# Revit family: CHECK ANTIRETORNO
name_source: partatom
category: Pipe Accessories
units: mm (PartAtom-declared; Revit-internal decimal feet)

## family parameters
Always vertical = Yes
Cut with Voids When Loaded = No
Part Type = Valve - Breaks Into
Round Connector Dimension = Use Diameter
Shared = No
Work Plane-Based = No

## types (2) — shared parameters
Description = VÁLVULA CHECK ANTI-RETORNO EN PVC
Imagen = https://pcpplasticos.co
Manufacturer = PCP PLASTICOS
URL = https://pcpplasticos.co
zero-valued in all types: Default Elevation

## per-type parameters (varying)
| type | 4" | 6" | D | Model | SKU | d1 | d2 |
| Diametro 4" | Yes | No | 101.6 mm  [stored 0.333333 ft] | 3148 | 3148 | 135 mm  [stored 0.442913 ft] | 134.2 mm |
| Diametro 6" | No | Yes | 152.4 mm  [stored 0.5 ft] | 3377 | 3377 | 197.5 mm  [stored 0.647966 ft] | 196.7 mm  [stored 0.645341 ft] |

note: [stored X ft] marks values corroborated as IEEE doubles in the binary element streams (Revit-internal decimal feet)

## geometry (parser evidence)
native form markers: Sweep x3
no freeform markers — native parametric forms only
